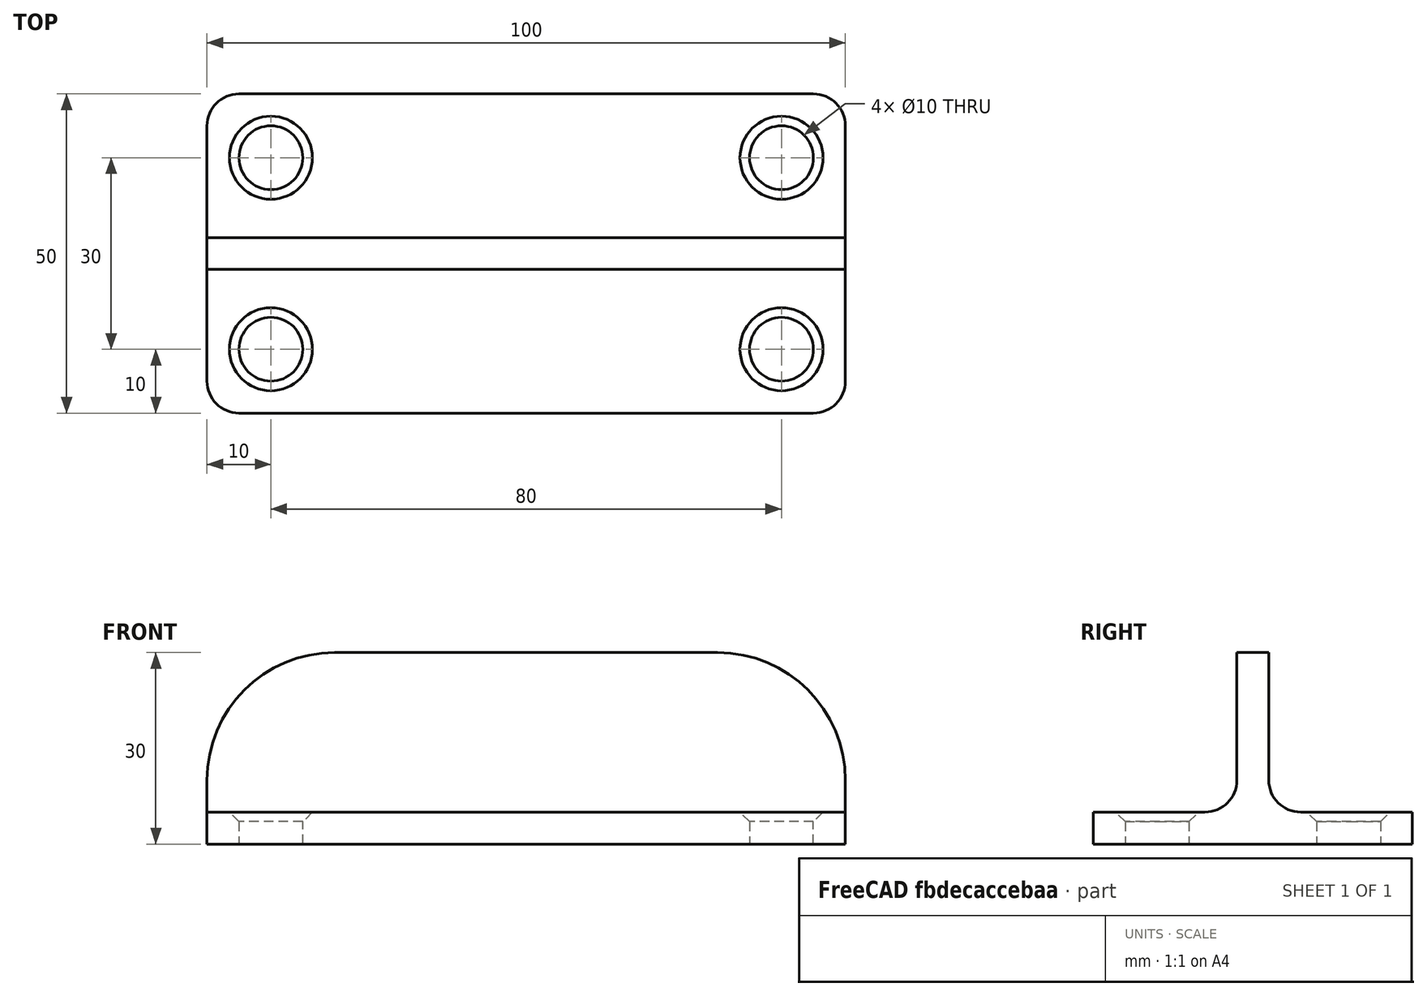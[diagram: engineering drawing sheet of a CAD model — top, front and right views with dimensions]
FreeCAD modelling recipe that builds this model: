
FCSTD DOCUMENT  (FreeCAD 1.0R39319 (Git))
Label: tutor2
License: All rights reserved
LicenseURL: https://en.wikipedia.org/wiki/All_rights_reserved
objects: TechDraw::DrawViewDimension×7, TechDraw::DrawProjGroupItem×4, Sketcher::SketchObject×2, PartDesign::Pad×2, PartDesign::Fillet×1, PartDesign::Chamfer×1, PartDesign::Body×1, TechDraw::DrawSVGTemplate×1, TechDraw::DrawProjGroup×1, TechDraw::DrawRichAnno×1, TechDraw::DrawViewAnnotation×1, TechDraw::DrawPage×1
note: 28 computed .brp shape members not serialized (recipe doc carries the construction recipe); baked Part::Feature solids carry a one-line shape summary decoded from their .brp

FEATURE [Sketcher::SketchObject] Sketch
  ArcFitTolerance = 1e-06
  AttachmentSupport = -> [XY_Plane]
  FullyConstrained = true
  MakeInternals = false
  MapMode = 5
  sketch-geometry (17):
    g0: LineSegment StartX=-50 StartY=20 StartZ=0 EndX=-50 EndY=-20 EndZ=0
    g1: LineSegment StartX=-45 StartY=-25 StartZ=0 EndX=45 EndY=-25 EndZ=0
    g2: LineSegment StartX=50 StartY=-20 StartZ=0 EndX=50 EndY=20 EndZ=0
    g3: LineSegment StartX=45 StartY=25 StartZ=0 EndX=-45 EndY=25 EndZ=0
    g4: GeomPoint [constr] X=0 Y=0 Z=0
    g5: Circle CenterX=-40 CenterY=15 CenterZ=0 NormalX=0 NormalY=0 NormalZ=1 AngleXU=0 Radius=5
    g6: Circle CenterX=40 CenterY=15 CenterZ=0 NormalX=0 NormalY=0 NormalZ=1 AngleXU=0 Radius=5
    g7: Circle CenterX=40 CenterY=-15 CenterZ=0 NormalX=0 NormalY=0 NormalZ=1 AngleXU=0 Radius=5
    g8: Circle CenterX=-40 CenterY=-15 CenterZ=0 NormalX=0 NormalY=0 NormalZ=1 AngleXU=0 Radius=5
    g9: ArcOfCircle CenterX=-45 CenterY=-20 CenterZ=0 NormalX=0 NormalY=0 NormalZ=1 AngleXU=0 Radius=5 StartAngle=3.14159 EndAngle=4.71239
    g10: GeomPoint [constr] X=-50 Y=-25 Z=0
    g11: ArcOfCircle CenterX=45 CenterY=-20 CenterZ=0 NormalX=0 NormalY=0 NormalZ=1 AngleXU=0 Radius=5 StartAngle=4.71239 EndAngle=6.28319
    g12: GeomPoint [constr] X=50 Y=-25 Z=0
    g13: ArcOfCircle CenterX=45 CenterY=20 CenterZ=0 NormalX=0 NormalY=0 NormalZ=1 AngleXU=0 Radius=5 StartAngle=0 EndAngle=1.5708
    g14: GeomPoint [constr] X=50 Y=25 Z=0
    g15: ArcOfCircle CenterX=-45 CenterY=20 CenterZ=0 NormalX=0 NormalY=0 NormalZ=1 AngleXU=0 Radius=5 StartAngle=1.5708 EndAngle=3.14159
    g16: GeomPoint [constr] X=-50 Y=25 Z=0
  constraints (38):
    c: Vertical(g0)
    c: Vertical(g2)
    c: Horizontal(g1)
    c: Horizontal(g3)
    c: Symmetric(g12,g16,g4)
    c: Coincident(g4,g-1)
    c: DistanceX(g16,g14) = 100
    c: DistanceY(g12,g14) = 50
    c: Equal(g5,g6)
    c: Equal(g5,g7)
    c: Equal(g5,g8)
    c: Diameter(g5) = 10
    c: Symmetric(g5,g6,g-2)
    c: Symmetric(g8,g5,g-1)
    c: Vertical(g7,g6)
    c: Horizontal(g8,g7)
    c: DistanceX(g16,g5) = 10
    c: DistanceY(g5,g16) = 10
    c: PointOnObject(g10,g1)
    c: PointOnObject(g10,g0)
    c: Tangent(g1,g9) = -1.5708
    c: Tangent(g0,g9) = -1.5708
    c: PointOnObject(g12,g1)
    c: PointOnObject(g12,g2)
    c: Tangent(g1,g11) = -1.5708
    c: Tangent(g2,g11) = -1.5708
    c: PointOnObject(g14,g2)
    c: PointOnObject(g14,g3)
    c: Tangent(g2,g13) = -1.5708
    c: Tangent(g3,g13) = -1.5708
    c: PointOnObject(g16,g0)
    c: PointOnObject(g16,g3)
    c: Tangent(g0,g15) = -1.5708
    c: Tangent(g3,g15) = -1.5708
    c: Equal(g15,g13)
    c: Equal(g15,g11)
    c: Equal(g15,g9)
    c: Diameter(g15) = 10
FEATURE [PartDesign::Pad] Pad
  Direction = (0,0,1)
  Length = 5
  Length2 = 10
  Profile = -> Sketch
  ReferenceAxis = -> Sketch [N_Axis]
  Refine = true
  Suppressed = false
  Type = 0
FEATURE [Sketcher::SketchObject] Sketch001
  ArcFitTolerance = 1e-06
  AttachmentSupport = -> [XZ_Plane]
  ExternalGeometry = -> [Pad]
  FullyConstrained = true
  MakeInternals = false
  MapMode = 5
  Placement = pos=(0,0,0) rot=(1,0,0;1.5708rad)
  sketch-geometry (8):
    g0: LineSegment StartX=-50 StartY=10 StartZ=0 EndX=-50 EndY=5 EndZ=0
    g1: LineSegment StartX=-50 StartY=5 StartZ=0 EndX=50 EndY=5 EndZ=0
    g2: LineSegment StartX=50 StartY=5 StartZ=0 EndX=50 EndY=10 EndZ=0
    g3: LineSegment StartX=30 StartY=30 StartZ=0 EndX=-30 EndY=30 EndZ=0
    g4: ArcOfCircle CenterX=-30 CenterY=10 CenterZ=0 NormalX=0 NormalY=0 NormalZ=1 AngleXU=0 Radius=20 StartAngle=1.5708 EndAngle=3.14159
    g5: GeomPoint [constr] X=-50 Y=30 Z=0
    g6: ArcOfCircle CenterX=30 CenterY=10 CenterZ=0 NormalX=0 NormalY=0 NormalZ=1 AngleXU=0 Radius=20 StartAngle=0 EndAngle=1.5708
    g7: GeomPoint [constr] X=50 Y=30 Z=0
  constraints (18):
    c: Coincident(g0,g1)
    c: Coincident(g1,g2)
    c: Vertical(g0)
    c: Vertical(g2)
    c: Horizontal(g3)
    c: Coincident(g-3,g1)
    c: DistanceY(g0,g5) = 25
    c: Coincident(g-4,g0)
    c: PointOnObject(g5,g0)
    c: PointOnObject(g5,g3)
    c: Tangent(g0,g4) = -1.5708
    c: Tangent(g3,g4) = -1.5708
    c: PointOnObject(g7,g3)
    c: PointOnObject(g7,g2)
    c: Tangent(g3,g6) = -1.5708
    c: Tangent(g2,g6) = -1.5708
    c: Equal(g4,g6)
    c: Diameter(g4) = 40
FEATURE [PartDesign::Pad] Pad001
  BaseFeature = -> Pad
  Direction = (0,-1,2e-16)
  Length = 5
  Length2 = 10
  Midplane = true
  Profile = -> Sketch001
  ReferenceAxis = -> Sketch001 [N_Axis]
  Refine = true
  Suppressed = false
  Type = 0
FEATURE [PartDesign::Fillet] Fillet
  Base = -> Pad001 [Edge26,Edge22]
  BaseFeature = -> Pad001
  Radius = 5
  Refine = true
  SupportTransform = false
  Suppressed = false
  UseAllEdges = false
FEATURE [PartDesign::Chamfer] Chamfer
  Angle = 45
  Base = -> Fillet [Edge8,Edge7,Edge48,Edge47]
  BaseFeature = -> Fillet
  ChamferType = 0
  FlipDirection = false
  Refine = true
  Size = 1.5
  Size2 = 1
  SupportTransform = false
  Suppressed = false
  UseAllEdges = false
FEATURE [PartDesign::Body] Body
  AllowCompound = false
  Group = -> [Sketch,Pad,Sketch001,Pad001,Fillet,Chamfer]
  Origin = -> Origin
  Tip = -> Chamfer
FEATURE [TechDraw::DrawSVGTemplate] Template
  Height = 297
  Orientation = 0
  Template = C:/Program Files/FreeCAD 1.0/data/Mod/TechDraw/Templates/A4_Portrait_blank.svg
  Width = 210
FEATURE [TechDraw::DrawProjGroupItem] View  label="Front"
  CoarseView = false
  Direction = (0,-1,0)
  Focus = 100
  HardHidden = false
  IsoCount = 0
  IsoHidden = false
  IsoVisible = false
  LockPosition = true
  Perspective = false
  Rotation = 0
  RotationVector = (1,0,0)
  ScaleType = 2
  ScrubCount = 1
  SeamHidden = false
  SeamVisible = false
  SmoothHidden = false
  SmoothVisible = true
  Source = -> [Body]
  Type = 0
  X = 0
  XDirection = (1,0,0)
  Y = 0
FEATURE [TechDraw::DrawProjGroupItem] ProjItem004  label="Top"
  CoarseView = false
  Direction = (0,0,1)
  Focus = 100
  HardHidden = false
  IsoCount = 0
  IsoHidden = false
  IsoVisible = false
  LockPosition = false
  Perspective = false
  Rotation = 0
  RotationVector = (1,0,0)
  ScaleType = 0
  ScrubCount = 1
  SeamHidden = false
  SeamVisible = false
  SmoothHidden = false
  SmoothVisible = true
  Source = -> [Body]
  Type = 4
  X = 0
  XDirection = (1,0,0)
  Y = -55
FEATURE [TechDraw::DrawProjGroupItem] ProjItem006  label="Right"
  CoarseView = false
  Direction = (1,-1e-16,0)
  Focus = 100
  HardHidden = false
  IsoCount = 0
  IsoHidden = false
  IsoVisible = false
  LockPosition = false
  Perspective = false
  Rotation = 0
  RotationVector = (1,0,0)
  ScaleType = 0
  ScrubCount = 1
  SeamHidden = false
  SeamVisible = false
  SmoothHidden = false
  SmoothVisible = true
  Source = -> [Body]
  Type = 2
  X = -115.962
  XDirection = (1e-16,1,0)
  Y = 0
FEATURE [TechDraw::DrawProjGroupItem] ProjItem007  label="FrontBottomRight"
  CoarseView = false
  Direction = (0.57735,-0.57735,-0.57735)
  Focus = 100
  HardHidden = false
  IsoCount = 0
  IsoHidden = false
  IsoVisible = false
  LockPosition = false
  Perspective = false
  Rotation = 0
  RotationVector = (1,0,0)
  ScaleType = 0
  ScrubCount = 1
  SeamHidden = false
  SeamVisible = false
  SmoothHidden = false
  SmoothVisible = true
  Source = -> [Body]
  Type = 9
  X = -115.962
  XDirection = (0.707107,0.707107,0)
  Y = 64.5567
FEATURE [TechDraw::DrawProjGroup] ProjGroup
  Anchor = -> View
  AutoDistribute = true
  LockPosition = false
  ProjectionType = 0
  Rotation = 0
  ScaleType = 0
  Source = -> [Body]
  Views = -> [View,ProjItem004,ProjItem006,ProjItem007]
  X = 125.473
  Y = 138.298
  spacingX = 15
  spacingY = 15
FEATURE [TechDraw::DrawViewDimension] Dimension
  AngleOverride = false
  Arbitrary = false
  ArbitraryTolerances = false
  BoxCorners = (2) [(-50,-25,-1e-07),(50,25,1e-07)]
  EqualTolerance = true
  ExtensionAngle = 0
  FormatSpec = %.2w
  FormatSpecOverTolerance = %+.2w
  FormatSpecUnderTolerance = %+.2w
  Inverted = false
  LineAngle = 0
  LockPosition = false
  MeasureType = 1
  OverTolerance = 0
  References2D = -> [ProjItem004]
  Rotation = 0
  ScaleType = 0
  TheoreticalExact = false
  Type = 1
  UnderTolerance = 0
  X = 0
  Y = -39.7137
FEATURE [TechDraw::DrawViewDimension] Dimension001
  AngleOverride = false
  Arbitrary = false
  ArbitraryTolerances = false
  BoxCorners = (2) [(-50,-25,-1e-07),(50,25,1e-07)]
  EqualTolerance = true
  ExtensionAngle = 0
  FormatSpec = %.2w
  FormatSpecOverTolerance = %+.2w
  FormatSpecUnderTolerance = %+.2w
  Inverted = false
  LineAngle = 0
  LockPosition = false
  MeasureType = 1
  OverTolerance = 0
  References2D = -> [ProjItem004]
  Rotation = 0
  ScaleType = 0
  TheoreticalExact = false
  Type = 2
  UnderTolerance = 0
  X = 56.3186
  Y = 0
FEATURE [TechDraw::DrawViewDimension] Dimension002
  AngleOverride = false
  Arbitrary = false
  ArbitraryTolerances = false
  BoxCorners = (2) [(-50,-25,-1e-07),(50,25,1e-07)]
  EqualTolerance = true
  ExtensionAngle = 0
  FormatSpec = ⌀%.2w
  FormatSpecOverTolerance = %+.2w
  FormatSpecUnderTolerance = %+.2w
  Inverted = false
  LineAngle = 0
  LockPosition = false
  MeasureType = 1
  OverTolerance = 0
  References2D = -> [ProjItem004]
  Rotation = 0
  ScaleType = 0
  TheoreticalExact = false
  Type = 5
  UnderTolerance = 0
  X = 74.2274
  Y = -31.619
FEATURE [TechDraw::DrawViewDimension] Dimension003
  AngleOverride = false
  Arbitrary = false
  ArbitraryTolerances = false
  BoxCorners = (2) [(-50,-25,-1e-07),(50,25,1e-07)]
  EqualTolerance = true
  ExtensionAngle = 0
  FormatSpec = ⌀%.2w
  FormatSpecOverTolerance = %+.2w
  FormatSpecUnderTolerance = %+.2w
  Inverted = false
  LineAngle = 0
  LockPosition = false
  MeasureType = 1
  OverTolerance = 0
  References2D = -> [ProjItem004]
  Rotation = 0
  ScaleType = 0
  TheoreticalExact = false
  Type = 5
  UnderTolerance = 0
  X = 75.577
  Y = -15.2311
FEATURE [TechDraw::DrawViewDimension] Dimension004
  AngleOverride = false
  Arbitrary = false
  ArbitraryTolerances = false
  BoxCorners = (2) [(-50,-15,-1e-07),(50,15,1e-07)]
  EqualTolerance = true
  ExtensionAngle = 0
  FormatSpec = %.2w
  FormatSpecOverTolerance = %+.2w
  FormatSpecUnderTolerance = %+.2w
  Inverted = false
  LineAngle = 0
  LockPosition = false
  MeasureType = 1
  OverTolerance = 0
  References2D = -> [View]
  Rotation = 0
  ScaleType = 0
  TheoreticalExact = false
  Type = 2
  UnderTolerance = 0
  X = -63.4779
  Y = -12.5
FEATURE [TechDraw::DrawViewDimension] Dimension005
  AngleOverride = false
  Arbitrary = false
  ArbitraryTolerances = false
  BoxCorners = (2) [(-25,-15,-1e-07),(25,15,1e-07)]
  EqualTolerance = true
  ExtensionAngle = 0
  FormatSpec = %.2w
  FormatSpecOverTolerance = %+.2w
  FormatSpecUnderTolerance = %+.2w
  Inverted = false
  LineAngle = 0
  LockPosition = false
  MeasureType = 1
  OverTolerance = 0
  References2D = -> [ProjItem006]
  Rotation = 0
  ScaleType = 0
  TheoreticalExact = false
  Type = 2
  UnderTolerance = 0
  X = -22.4814
  Y = 2.5
FEATURE [TechDraw::DrawViewDimension] Dimension006
  AngleOverride = false
  Arbitrary = false
  ArbitraryTolerances = false
  BoxCorners = (2) [(-25,-15,-1e-07),(25,15,1e-07)]
  EqualTolerance = true
  ExtensionAngle = 0
  FormatSpec = %.2w
  FormatSpecOverTolerance = %+.2w
  FormatSpecUnderTolerance = %+.2w
  Inverted = false
  LineAngle = 0
  LockPosition = false
  MeasureType = 1
  OverTolerance = 0
  References2D = -> [ProjItem006]
  Rotation = 0
  ScaleType = 0
  TheoreticalExact = false
  Type = 2
  UnderTolerance = 0
  X = 8.23609
  Y = 5
FEATURE [TechDraw::DrawRichAnno] RichTextAnnotation
  AnnoText = <!DOCTYPE HTML PUBLIC "-//W3C//DTD HTML 4.0//EN" "http://www.w3.org/TR/REC-html40/strict.dtd">\n<html><head><meta name="qrichtext" content="1" /><style type="text/css">\np, li { white-space: pre-wrap; }\n</style></head><body style=" font-family:'MS Shell Dlg 2'; font-size:7.8pt; font-weight:400; font-style:normal;">\n<p style=" margin-top:0px; margin-bottom:0px; margin-left:0px; margin-right:0px; -qt-block-indent:0; text-indent:0px;"><span style=" font-size:10pt;">for j in range(1,100):<br />    print('THIS IS MY PROJECT')</span></p></body></html>
  LockPosition = false
  MaxWidth = -1
  Rotation = 0
  ScaleType = 0
  ShowFrame = false
  X = 159.434
  Y = 253.182
FEATURE [TechDraw::DrawViewAnnotation] Annotation
  Font = osifont
  LineSpace = 100
  LockPosition = false
  MaxWidth = -1
  Rotation = 0
  ScaleType = 0
  Text = MY PROJECT
  TextSize = 16
  TextStyle = 0
  X = 147.8
  Y = 281.553
FEATURE [TechDraw::DrawPage] Page
  KeepUpdated = true
  NextBalloonIndex = 2
  ProjectionType = 0
  Template = -> Template
  Views = -> [ProjGroup,Dimension,Dimension001,Dimension002,Dimension003,Dimension004,Dimension005,Dimension006,RichTextAnnotation,Annotation]
